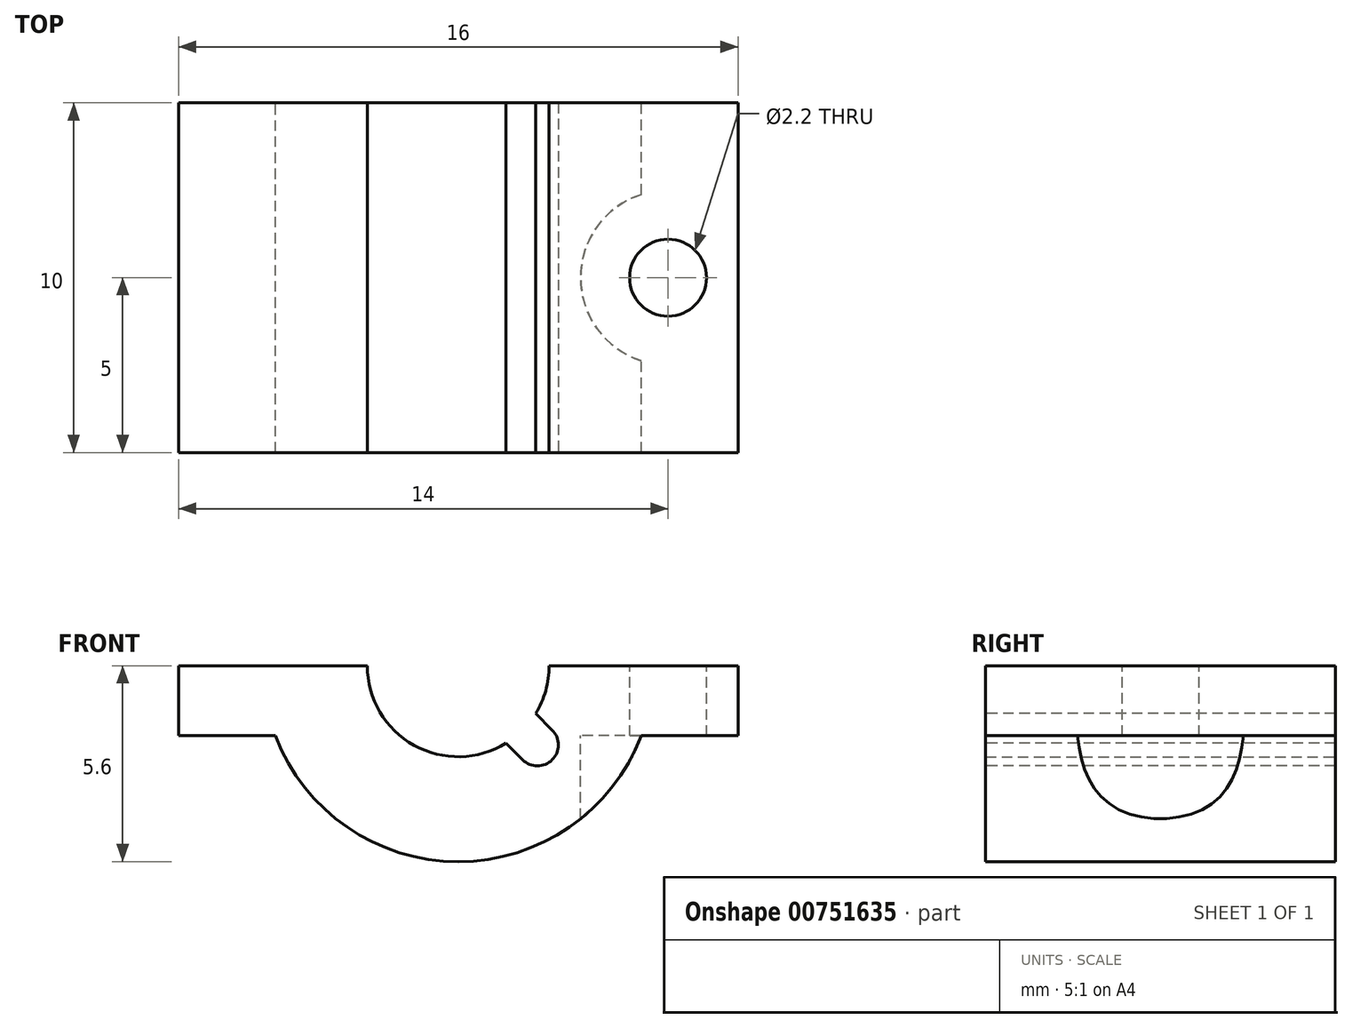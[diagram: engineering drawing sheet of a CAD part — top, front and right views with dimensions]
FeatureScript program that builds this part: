
annotation { "Feature Type Name" : "Feature", "Feature Type Description" : "" }
export const myFeature = defineFeature(function(context is Context, id is Id, definition is map)
    precondition{}
    {
        {
            var Q0;
            Q0=qCreatedBy(makeId("Front.planeOp"),FACE);
            var sketch = newSketch(context, id + "F0", { "sketchPlane" : qUnion([Q0])});
            skCircle(sketch, "E0", {"center": v(0, 0) * mm, "radius": 2.5 * mm});
            skSolve(sketch);
        }
        {
            var Q0;
            Q0=qCreatedBy(makeId("Front.planeOp"),FACE);
            var sketch = newSketch(context, id + "F1", { "sketchPlane" : qUnion([Q0])});
            skLineSegment(sketch, "E1", {"start": v(2.6, 0) * mm, "end": v(8, 0) * mm});
            skLineSegment(sketch, "E2", {"start": v(8, 0) * mm, "end": v(8, -2) * mm});
            skLineSegment(sketch, "E3", {"start": v(8, -2) * mm, "end": v(5.23, -2) * mm});
            skArc(sketch, "E4", {"start": v(2.6, 0) * mm, "mid": v(1.84, -1.84) * mm, "end": v(0, -2.6) * mm});
            skArc(sketch, "E5", {"start": v(5.23, -2) * mm, "mid": v(3.17, -4.61) * mm, "end": v(0, -5.6) * mm});
            skLineSegment(sketch, "E6", {"start": v(0, -2.6) * mm, "end": v(0, -5.6) * mm, "construction": true});
            skArc(sketch, "E7.MirrorCS", {"start": v(-2.6, 0) * mm, "mid": v(-1.84, -1.84) * mm, "end": v(0, -2.6) * mm});
            skArc(sketch, "E8.MirrorCS", {"start": v(-5.23, -2) * mm, "mid": v(-3.17, -4.61) * mm, "end": v(0, -5.6) * mm});
            skLineSegment(sketch, "E9.MirrorCS", {"start": v(-8, -2) * mm, "end": v(-5.23, -2) * mm});
            skLineSegment(sketch, "E10.MirrorCS", {"start": v(-8, 0) * mm, "end": v(-8, -2) * mm});
            skLineSegment(sketch, "E11.MirrorCS", {"start": v(-2.6, 0) * mm, "end": v(-8, 0) * mm});
            skSolve(sketch);
        }
        {
            var Q0;
            Q0 = qSketchRegion(id + "F1", true);
            extrude(context, id + "F2", {"entities" : qUnion([Q0]), "depth" : 10 * mm, "offsetDistance" : 25 * mm});
        }
        {
            var Q0;
            Q0=makeQuery(id+"F2.opExtrude","SWEPT_FACE",FACE,{"disambiguationData":[OSD([sQuery(id+"F1.wireOp",EDGE,"E1")])]});
            var sketch = newSketch(context, id + "F3", { "sketchPlane" : qUnion([Q0])});
            skCircle(sketch, "E12", {"center": v(6, -5) * mm, "radius": 1.1 * mm});
            skSolve(sketch);
        }
        {
            var Q0;
            Q0 = qSketchRegion(id + "F3", true);
            extrude(context, id + "F4", {"entities" : qUnion([Q0]), "operationType" : NewBodyOperationType.REMOVE, "oppositeDirection" : true, "depth" : 25 * mm, "offsetDistance" : 25 * mm});
        }
        {
            var Q0;
            Q0=makeQuery(id+"F2.opExtrude","SWEPT_FACE",FACE,{"disambiguationData":[OSD([sQuery(id+"F1.wireOp",EDGE,"E3")])]});
            var sketch = newSketch(context, id + "F5", { "sketchPlane" : qUnion([Q0])});
            skCircle(sketch, "E13", {"center": v(6, 5) * mm, "radius": 2.5 * mm});
            skSolve(sketch);
        }
        {
            var Q0;
            Q0 = qSketchRegion(id + "F5", true);
            extrude(context, id + "F6", {"entities" : qUnion([Q0]), "operationType" : NewBodyOperationType.REMOVE, "depth" : 25 * mm, "offsetDistance" : 25 * mm});
        }
        {
            var Q0;
            Q0=makeQuery(id+"F2.opExtrude","CAP_FACE",FACE,{"disambiguationData":[OSD([sQuery(id+"F1.wireOp",EDGE,"E1"),sQuery(id+"F1.wireOp",EDGE,"E2"),sQuery(id+"F1.wireOp",EDGE,"E3"),sQuery(id+"F1.wireOp",EDGE,"E4"),sQuery(id+"F1.wireOp",EDGE,"E5"),sQuery(id+"F1.wireOp",EDGE,"E7.MirrorCS"),sQuery(id+"F1.wireOp",EDGE,"E8.MirrorCS"),sQuery(id+"F1.wireOp",EDGE,"E9.MirrorCS"),sQuery(id+"F1.wireOp",EDGE,"E10.MirrorCS"),sQuery(id+"F1.wireOp",EDGE,"E11.MirrorCS")])],"isStart":false});
            var sketch = newSketch(context, id + "F7", { "sketchPlane" : qUnion([Q0])});
            skLineSegment(sketch, "E14", {"start": v(0, 0) * mm, "end": v(2.26, -2.26) * mm, "construction": true});
            skLineSegment(sketch, "E15", {"start": v(1.84, -2.69) * mm, "end": v(2.69, -1.84) * mm, "construction": true});
            skArc(sketch, "E16", {"start": v(2.69, -1.84) * mm, "mid": v(2.69, -2.69) * mm, "end": v(1.84, -2.69) * mm});
            skLineSegment(sketch, "E17", {"start": v(2.69, -1.84) * mm, "end": v(2.21, -1.36) * mm});
            skLineSegment(sketch, "E18", {"start": v(1.84, -2.69) * mm, "end": v(1.36, -2.21) * mm});
            skLineSegment(sketch, "E19", {"start": v(1.36, -2.21) * mm, "end": v(2.21, -1.36) * mm});
            skSolve(sketch);
        }
        {
            var Q0;
            Q0 = qSketchRegion(id + "F7", true);
            extrude(context, id + "F8", {"entities" : qUnion([Q0]), "operationType" : NewBodyOperationType.REMOVE, "oppositeDirection" : true, "depth" : 25 * mm, "offsetDistance" : 25 * mm});
        }
        {
            var Q0;
            Q0=makeQuery(id+"F2.opExtrude","SWEPT_FACE",FACE,{"disambiguationData":[OSD([sQuery(id+"F1.wireOp",EDGE,"E11.MirrorCS")])]});
            cPlane(context, id + "F9", {"entities" : qUnion([Q0]), "cplaneType" : CPlaneType.OFFSET, "offset" : 6.5 * mm, "oppositeDirection" : true, "width" : 150 * mm, "height" : 150 * mm});
        }
        {
            var Q0;
            Q0=qCreatedBy(makeId("Right.planeOp"),FACE);
            cPlane(context, id + "F10", {"entities" : qUnion([Q0]), "cplaneType" : CPlaneType.OFFSET, "offset" : 2 * mm, "width" : 150 * mm, "height" : 150 * mm});
        }
    });
